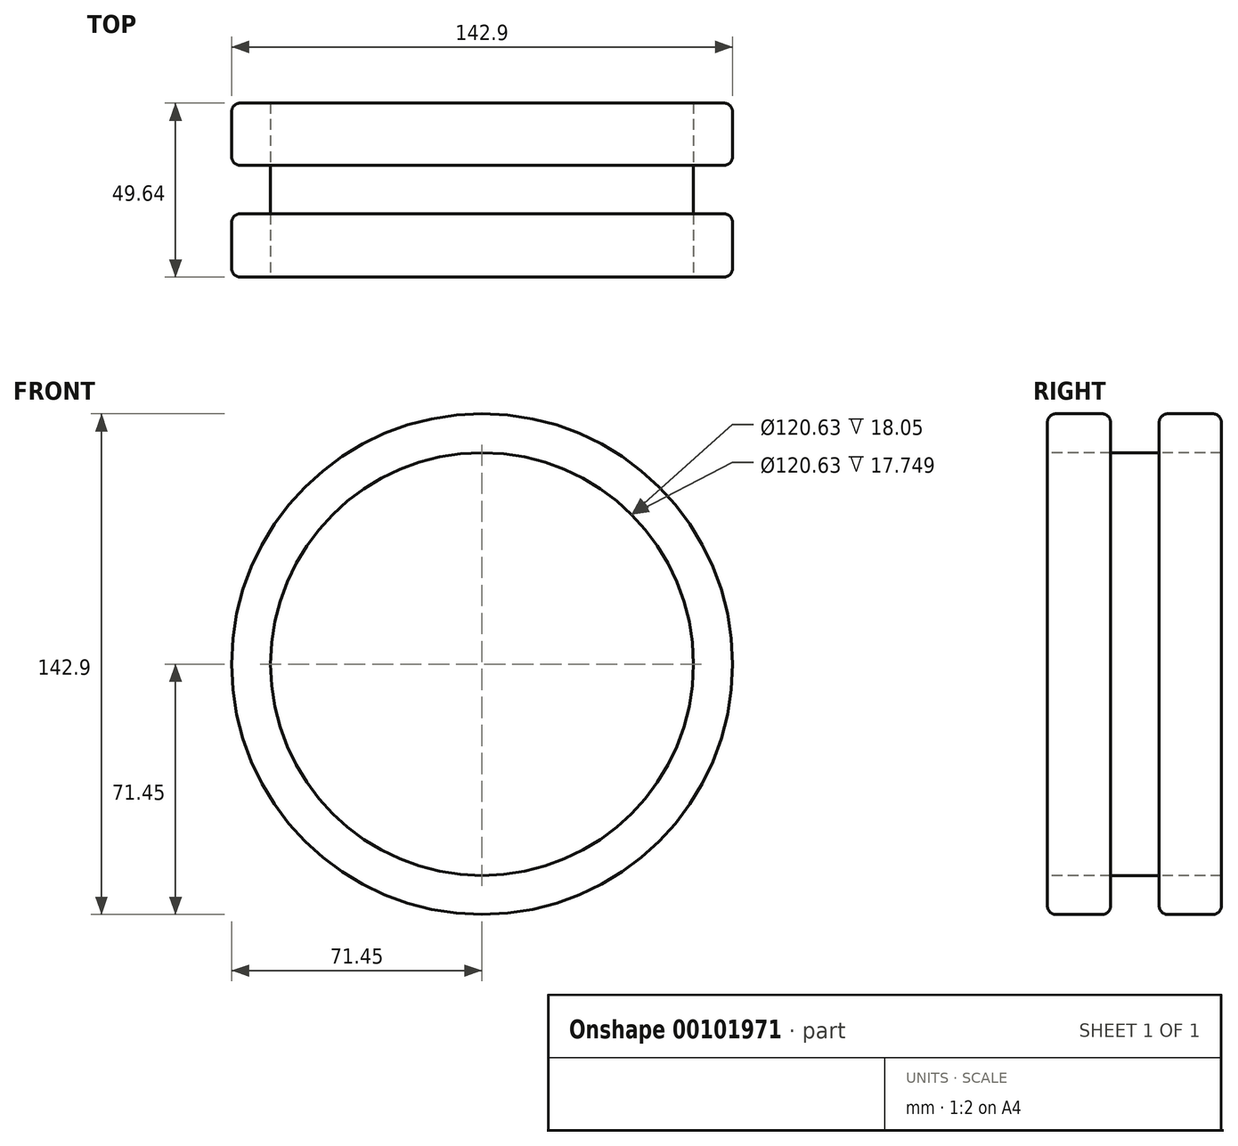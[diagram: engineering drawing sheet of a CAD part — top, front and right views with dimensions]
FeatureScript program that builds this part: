
annotation { "Feature Type Name" : "Feature", "Feature Type Description" : "" }
export const myFeature = defineFeature(function(context is Context, id is Id, definition is map)
    precondition{}
    {
        {
            var Q0;
            Q0=qCreatedBy(makeId("Right.planeOp"),FACE);
            var sketch = newSketch(context, id + "F0", { "sketchPlane" : qUnion([Q0])});
            skLineSegment(sketch, "E0.bottom", {"start": v(-53.25, 0) * mm, "end": v(-35.2, 0) * mm});
            skLineSegment(sketch, "E0.top", {"start": v(-53.25, 71.45) * mm, "end": v(-35.2, 71.45) * mm});
            skLineSegment(sketch, "E0.left", {"start": v(-53.25, 0) * mm, "end": v(-53.25, 71.45) * mm});
            skLineSegment(sketch, "E0.right", {"start": v(-35.2, 0) * mm, "end": v(-35.2, 71.45) * mm});
            skLineSegment(sketch, "E1.bottom", {"start": v(-53.25, 0) * mm, "end": v(-3.6, 0) * mm});
            skLineSegment(sketch, "E1.top", {"start": v(-53.25, 60.32) * mm, "end": v(-3.6, 60.32) * mm});
            skLineSegment(sketch, "E1.left", {"start": v(-53.25, 0) * mm, "end": v(-53.25, 60.32) * mm});
            skLineSegment(sketch, "E1.right", {"start": v(-3.6, 0) * mm, "end": v(-3.6, 60.32) * mm});
            skLineSegment(sketch, "E2.bottom", {"start": v(-3.6, 0) * mm, "end": v(-21.36, 0) * mm});
            skLineSegment(sketch, "E2.top", {"start": v(-3.6, 71.45) * mm, "end": v(-21.36, 71.45) * mm});
            skLineSegment(sketch, "E2.left", {"start": v(-3.6, 0) * mm, "end": v(-3.6, 71.45) * mm});
            skLineSegment(sketch, "E2.right", {"start": v(-21.36, 0) * mm, "end": v(-21.36, 71.45) * mm});
            skSolve(sketch);
        }
        {
            var Q0;
            {var subQ5=sQuery(id+"F0.wireOp",EDGE,"E1.left");Q0=makeQuery(id+"F0.imprint","IMPRINT",FACE,{"disambiguationData":[TD([[makeQuery(id+"F0.imprint","IMPRINT",EDGE,{"derivedFrom":subQ5}),-1.0]])]});}
            var Q1;
            {var subQ0=sQuery(id+"F0.wireOp",EDGE,"E1.bottom");var subQ1=sQuery(id+"F0.wireOp",EDGE,"E0.right");var subQ2=makeQuery(id+"F0.imprint","INTERSECT",VERTEX,{"derivedFrom":[subQ1,subQ0]});Q1=makeQuery(id+"F0.imprint","IMPRINT",FACE,{"disambiguationData":[TD([[makeQuery(id+"F0.imprint","IMPRINT",EDGE,{"disambiguationData":[TD([[subQ2,-1.0]])],"derivedFrom":subQ1}),-1.0]])]});}
            var Q2;
            {var subQ5=sQuery(id+"F0.wireOp",EDGE,"E2.bottom");Q2=makeQuery(id+"F0.imprint","IMPRINT",FACE,{"disambiguationData":[TD([[makeQuery(id+"F0.imprint","IMPRINT",EDGE,{"derivedFrom":subQ5}),-1.0]])]});}
            var Q3;
            {var subQ5=sQuery(id+"F0.wireOp",EDGE,"E2.top");Q3=makeQuery(id+"F0.imprint","IMPRINT",FACE,{"disambiguationData":[TD([[makeQuery(id+"F0.imprint","IMPRINT",EDGE,{"derivedFrom":subQ5}),1.0]])]});}
            var Q4;
            {var subQ0=sQuery(id+"F0.wireOp",EDGE,"E0.top");Q4=makeQuery(id+"F0.imprint","IMPRINT",FACE,{"disambiguationData":[TD([[makeQuery(id+"F0.imprint","IMPRINT",EDGE,{"derivedFrom":subQ0}),-1.0]])]});}
            var Q5;
            Q5=sQuery(id+"F0.wireOp",EDGE,"E1.bottom");
            revolve(context, id + "F1", {"entities" : qUnion([Q0, Q1, Q2, Q3, Q4]), "axis" : qUnion([Q5]), "revolveType" : RevolveType.FULL});
        }
        {
            var Q0;
            Q0=makeQuery(id+"F1.opRevolve","SWEPT_EDGE",EDGE,{"disambiguationData":[OSD([sQuery(id+"F0.wireOp",EDGE,"E0.top"),sQuery(id+"F0.wireOp",EDGE,"E0.right")])]});
            fillet(context, id + "F2", {"entities" : qUnion([Q0]), "radius" : 2.5 * mm, "tangentPropagation" : true, "allowEdgeOverflow" : false});
        }
        {
            var Q0;
            Q0=makeQuery(id+"F1.opRevolve","SWEPT_EDGE",EDGE,{"disambiguationData":[OSD([sQuery(id+"F0.wireOp",EDGE,"E2.top"),sQuery(id+"F0.wireOp",EDGE,"E2.right")])]});
            fillet(context, id + "F3", {"entities" : qUnion([Q0]), "radius" : 2.5 * mm, "tangentPropagation" : true, "allowEdgeOverflow" : false});
        }
        {
            var Q0;
            Q0=makeQuery(id+"F1.opRevolve","SWEPT_EDGE",EDGE,{"disambiguationData":[OSD([sQuery(id+"F0.wireOp",EDGE,"E0.top"),sQuery(id+"F0.wireOp",EDGE,"E0.left")])]});
            fillet(context, id + "F4", {"entities" : qUnion([Q0]), "radius" : 2.5 * mm, "tangentPropagation" : true, "allowEdgeOverflow" : false});
        }
        {
            var Q0;
            Q0=makeQuery(id+"F1.opRevolve","SWEPT_EDGE",EDGE,{"disambiguationData":[OSD([sQuery(id+"F0.wireOp",EDGE,"E2.top"),sQuery(id+"F0.wireOp",EDGE,"E2.left")])]});
            fillet(context, id + "F5", {"entities" : qUnion([Q0]), "radius" : 2.5 * mm, "tangentPropagation" : true, "allowEdgeOverflow" : false});
        }
    });
